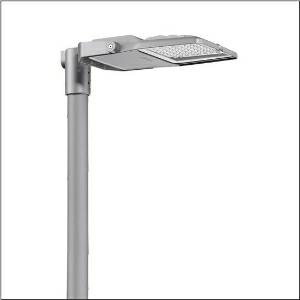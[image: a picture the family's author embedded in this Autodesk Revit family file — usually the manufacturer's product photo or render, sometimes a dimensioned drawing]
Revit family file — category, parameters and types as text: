
# Revit family: floodlight_fl_21_mini___pl43_5xa7775c2a3a_cdc0
name_source: partatom
category: Lighting Fixtures
units: mm (PartAtom-declared; Revit-internal decimal feet)

## family parameters
Cut with Voids When Loaded = No
Host = Face
Light Source = No
Part Type = Normal
Room Calculation Point = No
Round Connector Dimension = Use Diameter
Shared = No

## types (1)
- --- (1 x LED, 12500 lm, 89 W, 3000K)
    Apparent Load = 89 VA
    CIE Flux Codes = 27 78 99 100 100
    Color Rendering = 70
    Color Temperature = 3000K
    Default Elevation = 1800 mm
    Description = Floodlight FL 21 mini, floodlight, primary light control with lens, of PMMA, primary optical cover: protective disc, of toughened safety glass, transparent, light distribution: PL43, light emission: direct distribution, installation type: surface-mounted, LED, High Power LED, rated luminous flux: 12.500lm, luminous efficacy: 140lm/W, light colour: 730, colour temperature: 3000K, control gear: Smart Interface (Zhaga), control: flexible luminous flux parameterisation, time-dependent luminous flux control, constant luminous flux control, overheat protection, pre-setting: logarithmic dimming characteristic, with terminal, 6-pole, mains connection: 220..240V, AC, 50/60Hz, start of lifetime: 89W, end of service life: 94W, reduction: 43W, luminaire housing, of diecast aluminium, powder-coated, Siteco® metallic grey (DB 702S), corrosivity category C5 mid according to DIN EN ISO 12944, suitable for swimming pools, chlorine-resistant, sealing non-destructively replaceable, please order mast flange separately, mast bracket, of steel, galvanised, powder-coated, Siteco® metallic grey (DB 702S), Smart Interface above, protection rating (complete): IP66, insulation class (complete): insulation class II (safety insulation), certification: CE, ENEC, VDE, protection symbol: D, impact resistance: IK08, permissible operating ambient temperature: -40..+40°C, permissible operating ambient temperature for outdoor applications: -40..+50°C, standard: DIN EN 12944, LABS conformity tested according to VDMA 24364:2018-05, packaging unit: 1 piece

Light Distribution: PL43
    Height = 70 mm
    Lamp = 1 x LED
    Lamp Light Flux = 12500 lm
    Lamp Power = 89 W
    Lamp count = 1
    Length = 485 mm
    Luminous efficacy = 140 lm/W
    Manufacturer = Siteco
    ModVariant = No
    Model = 5XA7775C2A3A
    Number of Poles = 1
    OnlyDefault = Yes
    Power Factor = 1
    Product Name = Floodlight FL 21 mini | PL43
    Product group = floodlight | pylon annexe
    ProductGroupID = 6200
    Protection Class = Protection class II
    Protection Degree = IP 66
    RLX_Detail_Level = 1
    RLX_Emergency_Light_Flux = 0 lm
    RLX_Emergency_Type = 0
    RLX_Emergency_Type_DB = No
    RlxData = <blob elided: 100805 chars, md5=7cf4e4a4>
    Socket = socket
    Standby Power = 0 W
    System Light Flux = 12500 lm
    System Power = 89 W
    Type Comments = factory setting: luminous flux: 100 % | dim-lin: 254 | 456 mA
    Type Image = l_1007125.jpg
    URL = http://relux.com
    VarID = @adj_161128
    Voltage = 0 V
    Weight = 0.00 kg
    Width = 337 mm

## geometry (parser evidence)
native form markers: Blend x4, Sweep x12
no freeform markers — native parametric forms only
